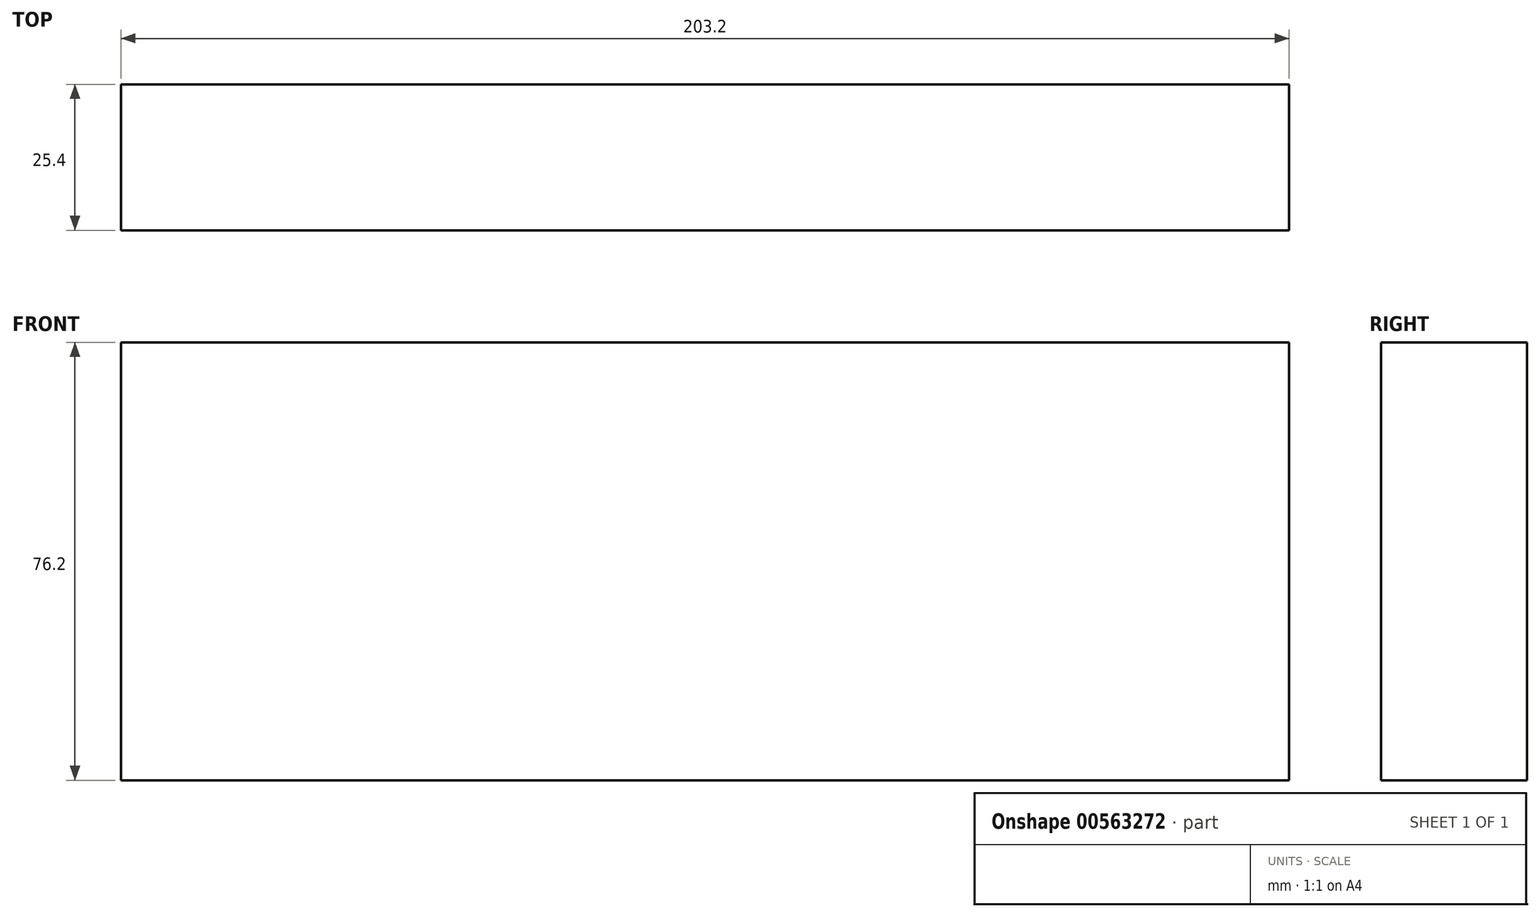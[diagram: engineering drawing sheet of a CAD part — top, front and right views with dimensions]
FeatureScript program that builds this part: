
annotation { "Feature Type Name" : "Feature", "Feature Type Description" : "" }
export const myFeature = defineFeature(function(context is Context, id is Id, definition is map)
    precondition{}
    {
        {
            var Q0;
            Q0=qCreatedBy(makeId("Top.planeOp"),FACE);
            var sketch = newSketch(context, id + "F0", { "sketchPlane" : qUnion([Q0])});
            skLineSegment(sketch, "E0.bottom", {"start": v(-7.51, 3.4) * mm, "end": v(195.69, 3.4) * mm});
            skLineSegment(sketch, "E0.top", {"start": v(-7.51, -22) * mm, "end": v(195.69, -22) * mm});
            skLineSegment(sketch, "E0.left", {"start": v(-7.51, 3.4) * mm, "end": v(-7.51, -22) * mm});
            skLineSegment(sketch, "E0.right", {"start": v(195.69, 3.4) * mm, "end": v(195.69, -22) * mm});
            skSolve(sketch);
        }
        {
            var Q0;
            Q0=makeQuery(id+"F0.imprint","IMPRINT",FACE,{"disambiguationData":[TD([[makeQuery(id+"F0.imprint","IMPRINT",EDGE,{"derivedFrom":sQuery(id+"F0.wireOp",EDGE,"E0.bottom")}),-1.0]])]});
            extrude(context, id + "F1", {"entities" : qUnion([Q0]), "depth" : 76.2 * mm, "offsetDistance" : 25.4 * mm});
        }
    });
